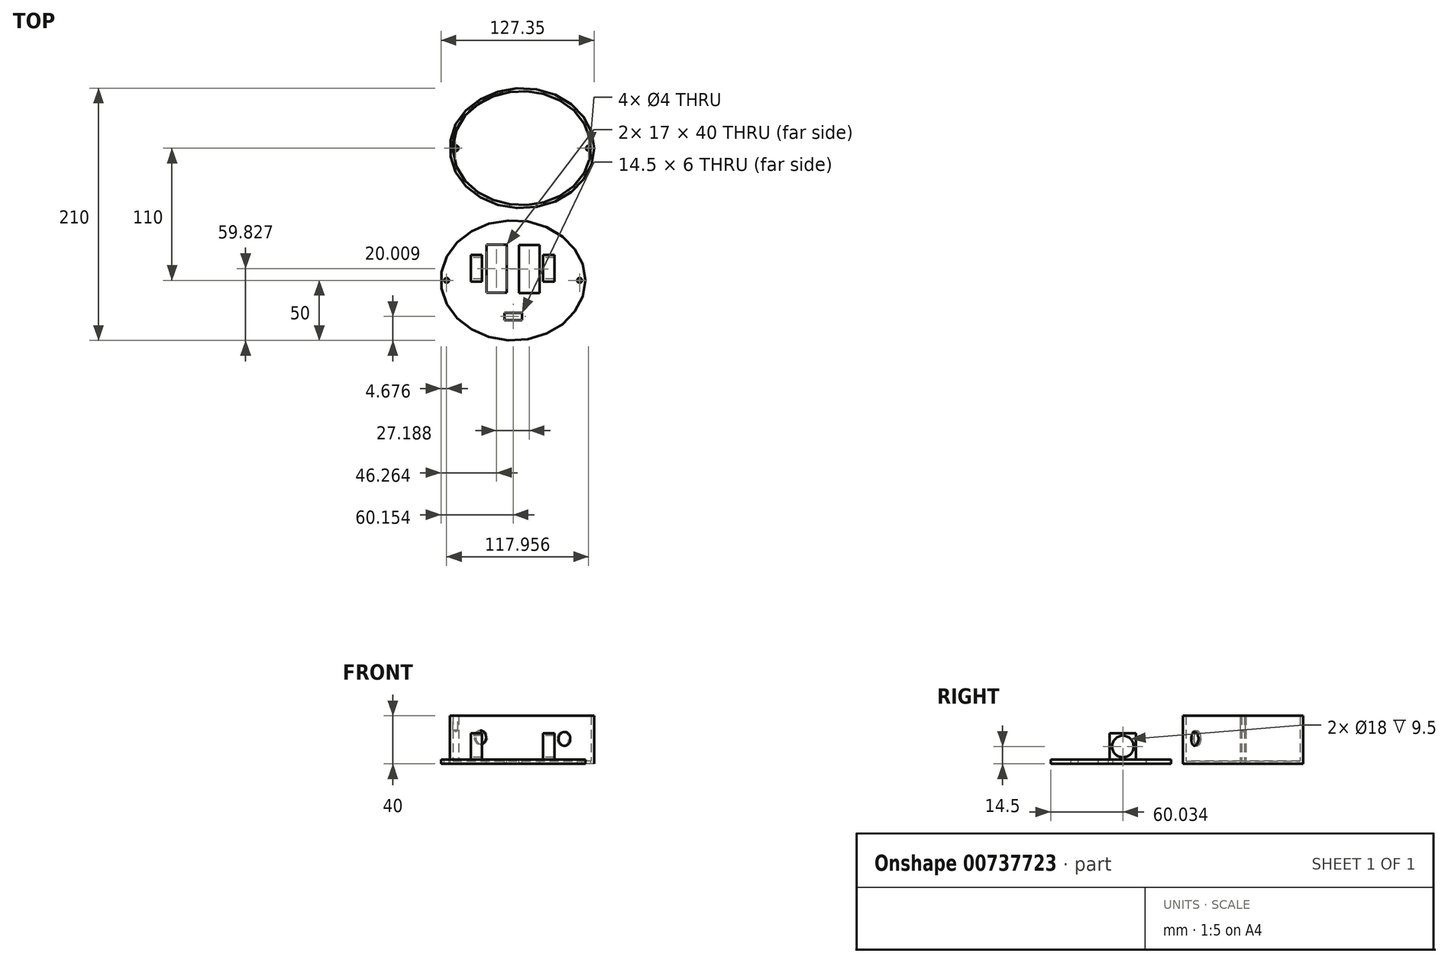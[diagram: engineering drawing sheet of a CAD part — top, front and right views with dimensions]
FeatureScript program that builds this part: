
annotation { "Feature Type Name" : "Feature", "Feature Type Description" : "" }
export const myFeature = defineFeature(function(context is Context, id is Id, definition is map)
    precondition{}
    {
        {
            var Q0;
            Q0=qCreatedBy(makeId("Top.planeOp"),FACE);
            var sketch = newSketch(context, id + "F0", { "sketchPlane" : qUnion([Q0])});
            skEllipse(sketch, "E0", {"center": v(0, 0) * mm, "majorRadius": 60 * mm, "minorRadius": 50 * mm, "majorAxis": v(1, 0)});
            skSolve(sketch);
        }
        {
            var Q0;
            Q0 = qSketchRegion(id + "F0", true);
            extrude(context, id + "F1", {"entities" : qUnion([Q0]), "depth" : 40 * mm, "offsetDistance" : 25 * mm});
        }
        {
            var Q0;
            Q0=makeQuery(id+"F1.opExtrude","CAP_FACE",FACE,{"disambiguationData":[OSD([sQuery(id+"F0.wireOp",EDGE,"E0")])],"isStart":false});
            shell(context, id + "F2", {"entities" : qUnion([Q0]), "thickness" : 2.5 * mm});
        }
        {
            var Q0;
            {var subQ0=sQuery(id+"F0.wireOp",EDGE,"E0");Q0=makeQuery(id+"F2.opShell","OFFSET_FACE",FACE,{"disambiguationData":[OSD([subQ0]),TDD([makeQuery(id+"F1.opExtrude","CAP_FACE",FACE,{"disambiguationData":[OSD([subQ0])],"isStart":true})])]});}
            var sketch = newSketch(context, id + "F3", { "sketchPlane" : qUnion([Q0])});
            skCircle(sketch, "E1", {"center": v(-55.28, 0) * mm, "radius": 2.5 * mm});
            skSolve(sketch);
        }
        {
            var Q0;
            Q0=makeQuery(id+"F3.imprint","IMPRINT",FACE,{"disambiguationData":[TD([[makeQuery(id+"F3.imprint","IMPRINT",EDGE,{"derivedFrom":sQuery(id+"F3.wireOp",EDGE,"E1")}),1.0]])]});
            var Q1;
            Q1 = qSketchRegion(id + "F3", true);
            extrude(context, id + "F4", {"entities" : qUnion([Q0, Q1]), "operationType" : NewBodyOperationType.ADD, "depth" : 37.5 * mm, "offsetDistance" : 25 * mm});
        }
        {
            var Q0;
            Q0=qCreatedBy(makeId("Top.planeOp"),FACE);
            var sketch = newSketch(context, id + "F5", { "sketchPlane" : qUnion([Q0])});
            skEllipse(sketch, "E2", {"center": v(-7.35, -110) * mm, "majorRadius": 60 * mm, "minorRadius": 50 * mm, "majorAxis": v(1, 0)});
            skSolve(sketch);
        }
        {
            var Q0;
            Q0=makeQuery(id+"F5.imprint","IMPRINT",FACE,{"disambiguationData":[TD([[makeQuery(id+"F5.imprint","IMPRINT",EDGE,{"derivedFrom":sQuery(id+"F5.wireOp",EDGE,"E2")}),1.0]])]});
            extrude(context, id + "F6", {"entities" : qUnion([Q0]), "depth" : 3.5 * mm, "offsetDistance" : 25 * mm});
        }
        {
            var Q0;
            Q0=qCreatedBy(makeId("Front.planeOp"),FACE);
            cPlane(context, id + "F7", {"entities" : qUnion([Q0]), "cplaneType" : CPlaneType.OFFSET, "offset" : 31 * mm, "width" : 150 * mm, "height" : 150 * mm});
        }
        {
            var Q0;
            Q0=qCreatedBy(id+"F7.planeOp",FACE);
            var sketch = newSketch(context, id + "F8", { "sketchPlane" : qUnion([Q0])});
            skLineSegment(sketch, "E3", {"start": v(29.98, 12.61) * mm, "end": v(29.98, 29.67) * mm});
            skSolve(sketch);
        }
        {
            var Q0;
            Q0=sQuery(id+"F8.wireOp",EDGE,"E3");
            cPlane(context, id + "F9", {"entities" : qUnion([Q0]), "cplaneType" : CPlaneType.LINE_ANGLE, "offset" : 25 * mm, "angle" : 60 * degree, "oppositeDirection" : true, "width" : 150 * mm, "height" : 150 * mm});
        }
        {
            var Q0;
            Q0=qCreatedBy(id+"F9.planeOp",FACE);
            var sketch = newSketch(context, id + "F10", { "sketchPlane" : qUnion([Q0])});
            skPoint(sketch, "E4", {"position": v(10.55, 20.81) * mm});
            skSolve(sketch);
        }
        {
            var Q0;
            Q0=sQuery(id+"F10.wireOp",VERTEX,"E4");
            var Q1;
            Q1=makeQuery(id+"F1.opExtrude","SWEPT_BODY",BODY,{"disambiguationData":[OSD([sQuery(id+"F0.wireOp",EDGE,"E0")])]});
            hole(context, id + "F11", {"style" : HoleStyle.SIMPLE, "endStyle" : HoleEndStyle.BLIND, "oppositeDirection" : true, "holeDiameter" : 11.5 * mm, "majorDiameter" : 5 * mm, "holeDepth" : 12 * mm, "isTappedThrough" : true, "tappedDepth" : 12 * mm, "tapClearance" : 3, "locations" : qUnion([Q0]), "scope" : qUnion([Q1])});
        }
        {
            var Q0;
            Q0=qCreatedBy(id+"F9.planeOp",FACE);
            var Q1;
            Q1=qCreatedBy(makeId("Right.planeOp"),FACE);
            cPlane(context, id + "F12", {"entities" : qUnion([Q0, Q1]), "cplaneType" : CPlaneType.MID_PLANE, "offset" : 25 * mm, "width" : 150 * mm, "height" : 150 * mm});
        }
        {
            var Q0;
            Q0=qCreatedBy(id+"F12.planeOp",FACE);
            var sketch = newSketch(context, id + "F13", { "sketchPlane" : qUnion([Q0])});
            skPoint(sketch, "E5", {"position": v(-9.83, 22.03) * mm});
            skSolve(sketch);
        }
        {
            var Q0;
            Q0=sQuery(id+"F13.wireOp",VERTEX,"E5");
            var Q1;
            Q1=makeQuery(id+"F1.opExtrude","SWEPT_BODY",BODY,{"disambiguationData":[OSD([sQuery(id+"F0.wireOp",EDGE,"E0")])]});
            hole(context, id + "F14", {"style" : HoleStyle.SIMPLE, "endStyle" : HoleEndStyle.BLIND, "oppositeDirection" : true, "holeDiameter" : 11.5 * mm, "majorDiameter" : 5 * mm, "holeDepth" : 12 * mm, "isTappedThrough" : true, "tappedDepth" : 12 * mm, "tapClearance" : 3, "locations" : qUnion([Q0]), "scope" : qUnion([Q1])});
        }
        {
            var Q0;
            Q0=qCreatedBy(makeId("Top.planeOp"),FACE);
            cPlane(context, id + "F15", {"entities" : qUnion([Q0]), "cplaneType" : CPlaneType.OFFSET, "offset" : 40 * mm, "width" : 150 * mm, "height" : 150 * mm});
        }
        {
            var Q0;
            Q0=makeQuery(id+"F6.opExtrude","CAP_FACE",FACE,{"disambiguationData":[OSD([sQuery(id+"F5.wireOp",EDGE,"E2")])],"isStart":false});
            var sketch = newSketch(context, id + "F16", { "sketchPlane" : qUnion([Q0])});
            skPoint(sketch, "E6", {"position": v(22.28, -99.97) * mm});
            skPoint(sketch, "E7", {"position": v(-37.87, -99.97) * mm});
            skLineSegment(sketch, "E8.bottom", {"start": v(-42.62, -88.97) * mm, "end": v(-33.12, -88.97) * mm});
            skLineSegment(sketch, "E8.top", {"start": v(-42.62, -110.97) * mm, "end": v(-33.12, -110.97) * mm});
            skLineSegment(sketch, "E8.left", {"start": v(-42.62, -88.97) * mm, "end": v(-42.62, -110.97) * mm});
            skLineSegment(sketch, "E8.right", {"start": v(-33.12, -88.97) * mm, "end": v(-33.12, -110.97) * mm});
            skLineSegment(sketch, "E9.bottom", {"start": v(17.53, -88.97) * mm, "end": v(27.03, -88.97) * mm});
            skLineSegment(sketch, "E9.top", {"start": v(17.53, -110.97) * mm, "end": v(27.03, -110.97) * mm});
            skLineSegment(sketch, "E9.left", {"start": v(17.53, -88.97) * mm, "end": v(17.53, -110.97) * mm});
            skLineSegment(sketch, "E9.right", {"start": v(27.03, -88.97) * mm, "end": v(27.03, -110.97) * mm});
            skLineSegment(sketch, "E10", {"start": v(-37.87, -99.97) * mm, "end": v(-35.59, -99.97) * mm});
            skLineSegment(sketch, "E11.bottom", {"start": v(14.6, -120.52) * mm, "end": v(-2.4, -120.52) * mm});
            skLineSegment(sketch, "E11.top", {"start": v(14.6, -80.52) * mm, "end": v(-2.4, -80.52) * mm});
            skLineSegment(sketch, "E11.left", {"start": v(14.6, -120.52) * mm, "end": v(14.6, -80.52) * mm});
            skLineSegment(sketch, "E11.right", {"start": v(-2.4, -120.52) * mm, "end": v(-2.4, -80.52) * mm});
            skLineSegment(sketch, "E12.bottom", {"start": v(-12.59, -120.17) * mm, "end": v(-29.59, -120.17) * mm});
            skLineSegment(sketch, "E12.top", {"start": v(-12.59, -80.17) * mm, "end": v(-29.59, -80.17) * mm});
            skLineSegment(sketch, "E12.left", {"start": v(-12.59, -120.17) * mm, "end": v(-12.59, -80.17) * mm});
            skLineSegment(sketch, "E12.right", {"start": v(-29.59, -120.17) * mm, "end": v(-29.59, -80.17) * mm});
            skLineSegment(sketch, "E13", {"start": v(-7.35, -160) * mm, "end": v(-7.35, -60) * mm});
            skCircle(sketch, "E14", {"center": v(52.65, -110) * mm, "radius": 4.7 * mm});
            skCircle(sketch, "E15", {"center": v(-67.35, -110) * mm, "radius": 4.7 * mm});
            skPoint(sketch, "E16", {"position": v(47.95, -110) * mm});
            skPoint(sketch, "E17", {"position": v(-62.67, -110) * mm});
            skSolve(sketch);
        }
        {
            var Q0;
            Q0=makeQuery(id+"F16.imprint","IMPRINT",FACE,{"disambiguationData":[TD([[makeQuery(id+"F16.imprint","IMPRINT",EDGE,{"derivedFrom":sQuery(id+"F16.wireOp",EDGE,"E8.bottom")}),-1.0]])]});
            var Q1;
            Q1=makeQuery(id+"F16.imprint","IMPRINT",FACE,{"disambiguationData":[TD([[makeQuery(id+"F16.imprint","IMPRINT",EDGE,{"derivedFrom":sQuery(id+"F16.wireOp",EDGE,"E9.bottom")}),-1.0]])]});
            extrude(context, id + "F17", {"entities" : qUnion([Q0, Q1]), "operationType" : NewBodyOperationType.ADD, "depth" : 22 * mm, "offsetDistance" : 25 * mm});
        }
        {
            var Q0;
            Q0=makeQuery(id+"F17.opExtrude","SWEPT_FACE",FACE,{"disambiguationData":[OSD([sQuery(id+"F16.wireOp",EDGE,"E8.left")])]});
            var sketch = newSketch(context, id + "F18", { "sketchPlane" : qUnion([Q0])});
            skLineSegment(sketch, "E18", {"start": v(110.97, 14.5) * mm, "end": v(88.97, 14.5) * mm});
            skLineSegment(sketch, "E19", {"start": v(99.97, 3.5) * mm, "end": v(99.97, 25.5) * mm});
            skPoint(sketch, "E20", {"position": v(99.97, 14.5) * mm});
            skSolve(sketch);
        }
        {
            var Q0;
            Q0=sQuery(id+"F18.wireOp",VERTEX,"E20");
            var Q1;
            Q1=makeQuery(id+"F6.opExtrude","SWEPT_BODY",BODY,{"disambiguationData":[OSD([sQuery(id+"F5.wireOp",EDGE,"E2")])]});
            hole(context, id + "F19", {"style" : HoleStyle.SIMPLE, "endStyle" : HoleEndStyle.THROUGH, "holeDiameter" : 18 * mm, "majorDiameter" : 5 * mm, "isTappedThrough" : true, "tappedDepth" : 12 * mm, "tapClearance" : 3, "locations" : qUnion([Q0]), "scope" : qUnion([Q1])});
        }
        {
            var Q0;
            Q0=makeQuery(id+"F16.imprint","IMPRINT",FACE,{"disambiguationData":[TD([[makeQuery(id+"F16.imprint","IMPRINT",EDGE,{"derivedFrom":sQuery(id+"F16.wireOp",EDGE,"E11.bottom")}),-1.0]])]});
            var Q1;
            Q1=makeQuery(id+"F16.imprint","IMPRINT",FACE,{"disambiguationData":[TD([[makeQuery(id+"F16.imprint","IMPRINT",EDGE,{"derivedFrom":sQuery(id+"F16.wireOp",EDGE,"E12.bottom")}),-1.0]])]});
            extrude(context, id + "F20", {"entities" : qUnion([Q0, Q1]), "operationType" : NewBodyOperationType.REMOVE, "oppositeDirection" : true, "depth" : 25 * mm, "offsetDistance" : 25 * mm});
        }
        {
            var Q0;
            {var subQ0=sQuery(id+"F3.wireOp",EDGE,"E1");Q0=makeQuery(id+"FTanrDDri6COW5f_1.1.F4.boolean.opBoolean","MERGE",FACE,{"derivedFrom":[makeQuery(id+"F4.boolean.opBoolean","MERGE",FACE,{"derivedFrom":[makeQuery(id+"F1.opExtrude","CAP_FACE",FACE,{"disambiguationData":[OSD([sQuery(id+"F0.wireOp",EDGE,"E0")])],"isStart":false}),makeQuery(id+"F4.opExtrude","CAP_FACE",FACE,{"disambiguationData":[OSD([subQ0])],"isStart":false})]}),makeQuery(id+"FTanrDDri6COW5f_1.1.F4.opExtrude","CAP_FACE",FACE,{"disambiguationData":[OSD([subQ0])],"isStart":false})]});}
            var sketch = newSketch(context, id + "F21", { "sketchPlane" : qUnion([Q0])});
            skPoint(sketch, "E21", {"position": v(-55.28, 0) * mm});
            skPoint(sketch, "E22", {"position": v(55.28, 0) * mm});
            skSolve(sketch);
        }
        {
            var Q0;
            Q0=sQuery(id+"F21.wireOp",VERTEX,"E22");
            var Q1;
            Q1=sQuery(id+"F21.wireOp",VERTEX,"E21");
            var Q2;
            Q2=makeQuery(id+"F1.opExtrude","SWEPT_BODY",BODY,{"disambiguationData":[OSD([sQuery(id+"F0.wireOp",EDGE,"E0")])]});
            hole(context, id + "F22", {"style" : HoleStyle.SIMPLE, "endStyle" : HoleEndStyle.BLIND, "holeDiameter" : 4 * mm, "majorDiameter" : 5 * mm, "holeDepth" : 12 * mm, "isTappedThrough" : true, "tappedDepth" : 12 * mm, "tapClearance" : 3, "locations" : qUnion([Q0, Q1]), "scope" : qUnion([Q2])});
        }
        {
            var Q0;
            Q0=sQuery(id+"F16.wireOp",VERTEX,"E16");
            var Q1;
            Q1=sQuery(id+"F16.wireOp",VERTEX,"E17");
            var Q2;
            Q2=makeQuery(id+"F6.opExtrude","SWEPT_BODY",BODY,{"disambiguationData":[OSD([sQuery(id+"F5.wireOp",EDGE,"E2")])]});
            hole(context, id + "F23", {"style" : HoleStyle.SIMPLE, "endStyle" : HoleEndStyle.THROUGH, "holeDiameter" : 4 * mm, "majorDiameter" : 5 * mm, "isTappedThrough" : true, "tappedDepth" : 12 * mm, "tapClearance" : 3, "locations" : qUnion([Q0, Q1]), "scope" : qUnion([Q2])});
        }
        {
            var Q0;
            Q0=makeQuery(id+"F16.imprint","IMPRINT",FACE,{"disambiguationData":[TD([[makeQuery(id+"F16.imprint","IMPRINT",EDGE,{"derivedFrom":sQuery(id+"F16.wireOp",EDGE,"E9.bottom")}),1.0]])]});
            var sketch = newSketch(context, id + "F24", { "sketchPlane" : qUnion([Q0])});
            skLineSegment(sketch, "E23.bottom", {"start": v(0.05, -143) * mm, "end": v(-14.45, -143) * mm});
            skLineSegment(sketch, "E23.top", {"start": v(0.05, -137) * mm, "end": v(-14.45, -137) * mm});
            skLineSegment(sketch, "E23.left", {"start": v(0.05, -143) * mm, "end": v(0.05, -137) * mm});
            skLineSegment(sketch, "E23.right", {"start": v(-14.45, -143) * mm, "end": v(-14.45, -137) * mm});
            skPoint(sketch, "E23.middle", {"position": v(-7.2, -140) * mm});
            skSolve(sketch);
        }
        {
            var Q0;
            Q0 = qSketchRegion(id + "F24", true);
            var Q1;
            Q1=makeQuery(id+"F24.imprint","IMPRINT",FACE,{"disambiguationData":[TD([[makeQuery(id+"F24.imprint","IMPRINT",EDGE,{"derivedFrom":sQuery(id+"F24.wireOp",EDGE,"E23.bottom")}),-1.0]])]});
            extrude(context, id + "F25", {"entities" : qUnion([Q0, Q1]), "operationType" : NewBodyOperationType.REMOVE, "oppositeDirection" : true, "depth" : 25 * mm, "offsetDistance" : 25 * mm});
        }
    });
